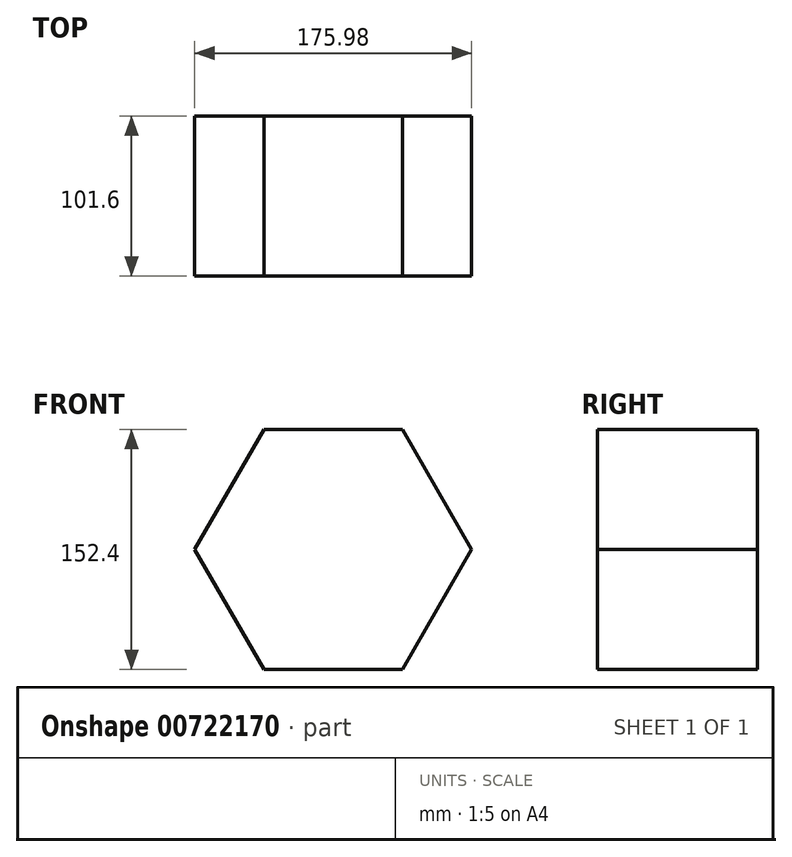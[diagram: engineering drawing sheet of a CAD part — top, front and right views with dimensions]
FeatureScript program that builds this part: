
annotation { "Feature Type Name" : "Feature", "Feature Type Description" : "" }
export const myFeature = defineFeature(function(context is Context, id is Id, definition is map)
    precondition{}
    {
        {
            var Q0;
            Q0=qCreatedBy(makeId("Front.planeOp"),FACE);
            var sketch = newSketch(context, id + "F0", { "sketchPlane" : qUnion([Q0])});
            skCircle(sketch, "E0.cCircle", {"center": v(0, 0) * mm, "radius": 76.2 * mm, "construction": true});
            skLineSegment(sketch, "E0.0", {"start": v(87.99, 0) * mm, "end": v(44, -76.2) * mm});
            skLineSegment(sketch, "E0.1", {"start": v(44, -76.2) * mm, "end": v(-44, -76.2) * mm});
            skLineSegment(sketch, "E0.2", {"start": v(-44, -76.2) * mm, "end": v(-87.99, 0) * mm});
            skLineSegment(sketch, "E0.3", {"start": v(-87.99, 0) * mm, "end": v(-44, 76.2) * mm});
            skLineSegment(sketch, "E0.4", {"start": v(-44, 76.2) * mm, "end": v(44, 76.2) * mm});
            skLineSegment(sketch, "E0.5", {"start": v(44, 76.2) * mm, "end": v(87.99, 0) * mm});
            skPoint(sketch, "E0.0.midPoint", {"position": v(66, -38.1) * mm});
            skSolve(sketch);
        }
        {
            var Q0;
            Q0 = qSketchRegion(id + "F0", true);
            extrude(context, id + "F1", {"entities" : qUnion([Q0]), "depth" : 101.6 * mm, "offsetDistance" : 25.4 * mm});
        }
    });
